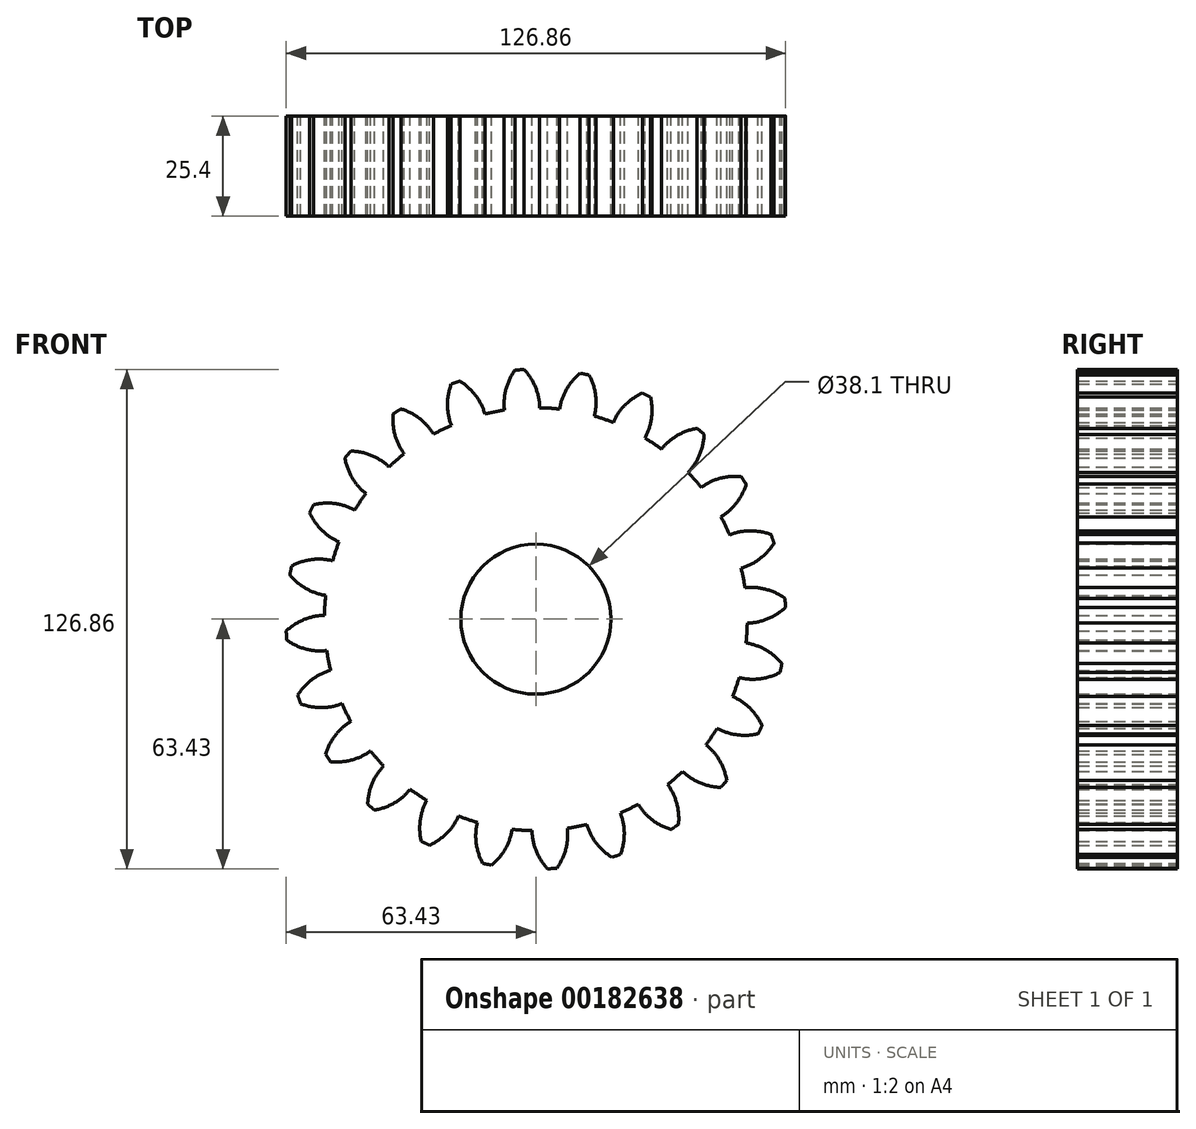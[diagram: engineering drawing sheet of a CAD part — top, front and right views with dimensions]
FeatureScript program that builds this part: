
annotation { "Feature Type Name" : "Feature", "Feature Type Description" : "" }
export const myFeature = defineFeature(function(context is Context, id is Id, definition is map)
    precondition{}
    {
        {
            var Q0;
            Q0=qCreatedBy(makeId("Front.planeOp"),FACE);
            var sketch = newSketch(context, id + "F0", { "sketchPlane" : qUnion([Q0])});
            skCircle(sketch, "E0", {"center": v(0, 0) * mm, "radius": 53.72 * mm});
            skCircle(sketch, "E1", {"center": v(0, 0) * mm, "radius": 58.67 * mm, "construction": true});
            skCircle(sketch, "E2", {"center": v(0, 0) * mm, "radius": 63.5 * mm, "construction": true});
            skLineSegment(sketch, "E3", {"start": v(0, 0) * mm, "end": v(0, 120.36) * mm, "construction": true});
            skLineSegment(sketch, "E4", {"start": v(0, 0) * mm, "end": v(-7.89, 120.36) * mm, "construction": true});
            skLineSegment(sketch, "E5", {"start": v(0, 58.67) * mm, "end": v(-98.12, 58.67) * mm, "construction": true});
            skLineSegment(sketch, "E6", {"start": v(0, 58.67) * mm, "end": v(-98.12, 22.96) * mm, "construction": true});
            skCircle(sketch, "E7", {"center": v(0, 0) * mm, "radius": 55.14 * mm, "construction": true});
            skCircle(sketch, "E8", {"center": v(0, 58.67) * mm, "radius": 14.6 * mm, "construction": true});
            skCircle(sketch, "E9", {"center": v(-13.63, 53.42) * mm, "radius": 14.6 * mm, "construction": true});
            skArc(sketch, "E10", {"start": v(0, 58.67) * mm, "mid": v(-1.27, 61.2) * mm, "end": v(-2.99, 63.43) * mm});
            skArc(sketch, "E11", {"start": v(0.97, 53.71) * mm, "mid": v(0.71, 56.24) * mm, "end": v(0, 58.67) * mm});
            skArc(sketch, "E12.MirrorCS", {"start": v(-7.98, 53.13) * mm, "mid": v(-8.05, 55.66) * mm, "end": v(-7.66, 58.17) * mm});
            skArc(sketch, "E13.MirrorCS", {"start": v(-7.66, 58.17) * mm, "mid": v(-6.72, 60.83) * mm, "end": v(-5.32, 63.28) * mm});
            skArc(sketch, "E14", {"start": v(-2.99, 63.43) * mm, "mid": v(-4.15, 63.36) * mm, "end": v(-5.32, 63.28) * mm});
            skSolve(sketch);
        }
        {
            var Q0;
            Q0=makeQuery(id+"F0.imprint","IMPRINT",FACE,{"disambiguationData":[TD([[makeQuery(id+"F0.imprint","IMPRINT",EDGE,{"derivedFrom":sQuery(id+"F0.wireOp",EDGE,"E10")}),1.0]])]});
            var Q1;
            {var subQ0=sQuery(id+"F0.wireOp",EDGE,"E0");var subQ1=makeQuery(id+"F0.imprint","INTERSECT",VERTEX,{"derivedFrom":[subQ0,sQuery(id+"F0.wireOp",EDGE,"E11")]});Q1=makeQuery(id+"F0.imprint","IMPRINT",FACE,{"disambiguationData":[TD([[makeQuery(id+"F0.imprint","IMPRINT",EDGE,{"disambiguationData":[TD([[subQ1,-1.0]])],"derivedFrom":subQ0}),1.0]])]});}
            extrude(context, id + "F1", {"entities" : qUnion([Q0, Q1]), "depth" : 25.4 * mm});
        }
        {
            var Q0;
            Q0=makeQuery(id+"F1.opExtrude","SWEPT_BODY",BODY,{"disambiguationData":[OSD([sQuery(id+"F0.wireOp",EDGE,"E0"),sQuery(id+"F0.wireOp",EDGE,"E10"),sQuery(id+"F0.wireOp",EDGE,"E11"),sQuery(id+"F0.wireOp",EDGE,"E12.MirrorCS"),sQuery(id+"F0.wireOp",EDGE,"E13.MirrorCS"),sQuery(id+"F0.wireOp",EDGE,"E14")])]});
            var Q1;
            Q1=makeQuery(id+"F1.opExtrude","SWEPT_FACE",FACE,{"disambiguationData":[OSD([sQuery(id+"F0.wireOp",EDGE,"E0")])]});
            circularPattern(context, id + "F2", {"entities" : qUnion([Q0]), "axis" : qUnion([Q1]), "angle" : 15 * degree, "instanceCount" : 24});
        }
        {
            var Q0;
            Q0=makeQuery(id+"F1.opExtrude","SWEPT_BODY",BODY,{"disambiguationData":[OSD([sQuery(id+"F0.wireOp",EDGE,"E0"),sQuery(id+"F0.wireOp",EDGE,"E10"),sQuery(id+"F0.wireOp",EDGE,"E11"),sQuery(id+"F0.wireOp",EDGE,"E12.MirrorCS"),sQuery(id+"F0.wireOp",EDGE,"E13.MirrorCS"),sQuery(id+"F0.wireOp",EDGE,"E14")])]});
            var Q1;
            Q1=makeQuery(id+"F2.opPattern","COPY",BODY,{"derivedFrom":makeQuery(id+"F1.opExtrude","SWEPT_BODY",BODY,{"disambiguationData":[OSD([sQuery(id+"F0.wireOp",EDGE,"E0"),sQuery(id+"F0.wireOp",EDGE,"E10"),sQuery(id+"F0.wireOp",EDGE,"E11"),sQuery(id+"F0.wireOp",EDGE,"E12.MirrorCS"),sQuery(id+"F0.wireOp",EDGE,"E13.MirrorCS"),sQuery(id+"F0.wireOp",EDGE,"E14")])]}),"instanceName":"1"});
            var Q2;
            Q2=makeQuery(id+"F2.opPattern","COPY",BODY,{"derivedFrom":makeQuery(id+"F1.opExtrude","SWEPT_BODY",BODY,{"disambiguationData":[OSD([sQuery(id+"F0.wireOp",EDGE,"E0"),sQuery(id+"F0.wireOp",EDGE,"E10"),sQuery(id+"F0.wireOp",EDGE,"E11"),sQuery(id+"F0.wireOp",EDGE,"E12.MirrorCS"),sQuery(id+"F0.wireOp",EDGE,"E13.MirrorCS"),sQuery(id+"F0.wireOp",EDGE,"E14")])]}),"instanceName":"2"});
            var Q3;
            Q3=makeQuery(id+"F2.opPattern","COPY",BODY,{"derivedFrom":makeQuery(id+"F1.opExtrude","SWEPT_BODY",BODY,{"disambiguationData":[OSD([sQuery(id+"F0.wireOp",EDGE,"E0"),sQuery(id+"F0.wireOp",EDGE,"E10"),sQuery(id+"F0.wireOp",EDGE,"E11"),sQuery(id+"F0.wireOp",EDGE,"E12.MirrorCS"),sQuery(id+"F0.wireOp",EDGE,"E13.MirrorCS"),sQuery(id+"F0.wireOp",EDGE,"E14")])]}),"instanceName":"3"});
            var Q4;
            Q4=makeQuery(id+"F2.opPattern","COPY",BODY,{"derivedFrom":makeQuery(id+"F1.opExtrude","SWEPT_BODY",BODY,{"disambiguationData":[OSD([sQuery(id+"F0.wireOp",EDGE,"E0"),sQuery(id+"F0.wireOp",EDGE,"E10"),sQuery(id+"F0.wireOp",EDGE,"E11"),sQuery(id+"F0.wireOp",EDGE,"E12.MirrorCS"),sQuery(id+"F0.wireOp",EDGE,"E13.MirrorCS"),sQuery(id+"F0.wireOp",EDGE,"E14")])]}),"instanceName":"4"});
            var Q5;
            Q5=makeQuery(id+"F2.opPattern","COPY",BODY,{"derivedFrom":makeQuery(id+"F1.opExtrude","SWEPT_BODY",BODY,{"disambiguationData":[OSD([sQuery(id+"F0.wireOp",EDGE,"E0"),sQuery(id+"F0.wireOp",EDGE,"E10"),sQuery(id+"F0.wireOp",EDGE,"E11"),sQuery(id+"F0.wireOp",EDGE,"E12.MirrorCS"),sQuery(id+"F0.wireOp",EDGE,"E13.MirrorCS"),sQuery(id+"F0.wireOp",EDGE,"E14")])]}),"instanceName":"5"});
            var Q6;
            Q6=makeQuery(id+"F2.opPattern","COPY",BODY,{"derivedFrom":makeQuery(id+"F1.opExtrude","SWEPT_BODY",BODY,{"disambiguationData":[OSD([sQuery(id+"F0.wireOp",EDGE,"E0"),sQuery(id+"F0.wireOp",EDGE,"E10"),sQuery(id+"F0.wireOp",EDGE,"E11"),sQuery(id+"F0.wireOp",EDGE,"E12.MirrorCS"),sQuery(id+"F0.wireOp",EDGE,"E13.MirrorCS"),sQuery(id+"F0.wireOp",EDGE,"E14")])]}),"instanceName":"6"});
            var Q7;
            Q7=makeQuery(id+"F2.opPattern","COPY",BODY,{"derivedFrom":makeQuery(id+"F1.opExtrude","SWEPT_BODY",BODY,{"disambiguationData":[OSD([sQuery(id+"F0.wireOp",EDGE,"E0"),sQuery(id+"F0.wireOp",EDGE,"E10"),sQuery(id+"F0.wireOp",EDGE,"E11"),sQuery(id+"F0.wireOp",EDGE,"E12.MirrorCS"),sQuery(id+"F0.wireOp",EDGE,"E13.MirrorCS"),sQuery(id+"F0.wireOp",EDGE,"E14")])]}),"instanceName":"7"});
            var Q8;
            Q8=makeQuery(id+"F2.opPattern","COPY",BODY,{"derivedFrom":makeQuery(id+"F1.opExtrude","SWEPT_BODY",BODY,{"disambiguationData":[OSD([sQuery(id+"F0.wireOp",EDGE,"E0"),sQuery(id+"F0.wireOp",EDGE,"E10"),sQuery(id+"F0.wireOp",EDGE,"E11"),sQuery(id+"F0.wireOp",EDGE,"E12.MirrorCS"),sQuery(id+"F0.wireOp",EDGE,"E13.MirrorCS"),sQuery(id+"F0.wireOp",EDGE,"E14")])]}),"instanceName":"8"});
            var Q9;
            Q9=makeQuery(id+"F2.opPattern","COPY",BODY,{"derivedFrom":makeQuery(id+"F1.opExtrude","SWEPT_BODY",BODY,{"disambiguationData":[OSD([sQuery(id+"F0.wireOp",EDGE,"E0"),sQuery(id+"F0.wireOp",EDGE,"E10"),sQuery(id+"F0.wireOp",EDGE,"E11"),sQuery(id+"F0.wireOp",EDGE,"E12.MirrorCS"),sQuery(id+"F0.wireOp",EDGE,"E13.MirrorCS"),sQuery(id+"F0.wireOp",EDGE,"E14")])]}),"instanceName":"9"});
            var Q10;
            Q10=makeQuery(id+"F2.opPattern","COPY",BODY,{"derivedFrom":makeQuery(id+"F1.opExtrude","SWEPT_BODY",BODY,{"disambiguationData":[OSD([sQuery(id+"F0.wireOp",EDGE,"E0"),sQuery(id+"F0.wireOp",EDGE,"E10"),sQuery(id+"F0.wireOp",EDGE,"E11"),sQuery(id+"F0.wireOp",EDGE,"E12.MirrorCS"),sQuery(id+"F0.wireOp",EDGE,"E13.MirrorCS"),sQuery(id+"F0.wireOp",EDGE,"E14")])]}),"instanceName":"10"});
            var Q11;
            Q11=makeQuery(id+"F2.opPattern","COPY",BODY,{"derivedFrom":makeQuery(id+"F1.opExtrude","SWEPT_BODY",BODY,{"disambiguationData":[OSD([sQuery(id+"F0.wireOp",EDGE,"E0"),sQuery(id+"F0.wireOp",EDGE,"E10"),sQuery(id+"F0.wireOp",EDGE,"E11"),sQuery(id+"F0.wireOp",EDGE,"E12.MirrorCS"),sQuery(id+"F0.wireOp",EDGE,"E13.MirrorCS"),sQuery(id+"F0.wireOp",EDGE,"E14")])]}),"instanceName":"11"});
            var Q12;
            Q12=makeQuery(id+"F2.opPattern","COPY",BODY,{"derivedFrom":makeQuery(id+"F1.opExtrude","SWEPT_BODY",BODY,{"disambiguationData":[OSD([sQuery(id+"F0.wireOp",EDGE,"E0"),sQuery(id+"F0.wireOp",EDGE,"E10"),sQuery(id+"F0.wireOp",EDGE,"E11"),sQuery(id+"F0.wireOp",EDGE,"E12.MirrorCS"),sQuery(id+"F0.wireOp",EDGE,"E13.MirrorCS"),sQuery(id+"F0.wireOp",EDGE,"E14")])]}),"instanceName":"12"});
            var Q13;
            Q13=makeQuery(id+"F2.opPattern","COPY",BODY,{"derivedFrom":makeQuery(id+"F1.opExtrude","SWEPT_BODY",BODY,{"disambiguationData":[OSD([sQuery(id+"F0.wireOp",EDGE,"E0"),sQuery(id+"F0.wireOp",EDGE,"E10"),sQuery(id+"F0.wireOp",EDGE,"E11"),sQuery(id+"F0.wireOp",EDGE,"E12.MirrorCS"),sQuery(id+"F0.wireOp",EDGE,"E13.MirrorCS"),sQuery(id+"F0.wireOp",EDGE,"E14")])]}),"instanceName":"13"});
            var Q14;
            Q14=makeQuery(id+"F2.opPattern","COPY",BODY,{"derivedFrom":makeQuery(id+"F1.opExtrude","SWEPT_BODY",BODY,{"disambiguationData":[OSD([sQuery(id+"F0.wireOp",EDGE,"E0"),sQuery(id+"F0.wireOp",EDGE,"E10"),sQuery(id+"F0.wireOp",EDGE,"E11"),sQuery(id+"F0.wireOp",EDGE,"E12.MirrorCS"),sQuery(id+"F0.wireOp",EDGE,"E13.MirrorCS"),sQuery(id+"F0.wireOp",EDGE,"E14")])]}),"instanceName":"14"});
            var Q15;
            Q15=makeQuery(id+"F2.opPattern","COPY",BODY,{"derivedFrom":makeQuery(id+"F1.opExtrude","SWEPT_BODY",BODY,{"disambiguationData":[OSD([sQuery(id+"F0.wireOp",EDGE,"E0"),sQuery(id+"F0.wireOp",EDGE,"E10"),sQuery(id+"F0.wireOp",EDGE,"E11"),sQuery(id+"F0.wireOp",EDGE,"E12.MirrorCS"),sQuery(id+"F0.wireOp",EDGE,"E13.MirrorCS"),sQuery(id+"F0.wireOp",EDGE,"E14")])]}),"instanceName":"15"});
            var Q16;
            Q16=makeQuery(id+"F2.opPattern","COPY",BODY,{"derivedFrom":makeQuery(id+"F1.opExtrude","SWEPT_BODY",BODY,{"disambiguationData":[OSD([sQuery(id+"F0.wireOp",EDGE,"E0"),sQuery(id+"F0.wireOp",EDGE,"E10"),sQuery(id+"F0.wireOp",EDGE,"E11"),sQuery(id+"F0.wireOp",EDGE,"E12.MirrorCS"),sQuery(id+"F0.wireOp",EDGE,"E13.MirrorCS"),sQuery(id+"F0.wireOp",EDGE,"E14")])]}),"instanceName":"16"});
            var Q17;
            Q17=makeQuery(id+"F2.opPattern","COPY",BODY,{"derivedFrom":makeQuery(id+"F1.opExtrude","SWEPT_BODY",BODY,{"disambiguationData":[OSD([sQuery(id+"F0.wireOp",EDGE,"E0"),sQuery(id+"F0.wireOp",EDGE,"E10"),sQuery(id+"F0.wireOp",EDGE,"E11"),sQuery(id+"F0.wireOp",EDGE,"E12.MirrorCS"),sQuery(id+"F0.wireOp",EDGE,"E13.MirrorCS"),sQuery(id+"F0.wireOp",EDGE,"E14")])]}),"instanceName":"17"});
            var Q18;
            Q18=makeQuery(id+"F2.opPattern","COPY",BODY,{"derivedFrom":makeQuery(id+"F1.opExtrude","SWEPT_BODY",BODY,{"disambiguationData":[OSD([sQuery(id+"F0.wireOp",EDGE,"E0"),sQuery(id+"F0.wireOp",EDGE,"E10"),sQuery(id+"F0.wireOp",EDGE,"E11"),sQuery(id+"F0.wireOp",EDGE,"E12.MirrorCS"),sQuery(id+"F0.wireOp",EDGE,"E13.MirrorCS"),sQuery(id+"F0.wireOp",EDGE,"E14")])]}),"instanceName":"18"});
            var Q19;
            Q19=makeQuery(id+"F2.opPattern","COPY",BODY,{"derivedFrom":makeQuery(id+"F1.opExtrude","SWEPT_BODY",BODY,{"disambiguationData":[OSD([sQuery(id+"F0.wireOp",EDGE,"E0"),sQuery(id+"F0.wireOp",EDGE,"E10"),sQuery(id+"F0.wireOp",EDGE,"E11"),sQuery(id+"F0.wireOp",EDGE,"E12.MirrorCS"),sQuery(id+"F0.wireOp",EDGE,"E13.MirrorCS"),sQuery(id+"F0.wireOp",EDGE,"E14")])]}),"instanceName":"19"});
            var Q20;
            Q20=makeQuery(id+"F2.opPattern","COPY",BODY,{"derivedFrom":makeQuery(id+"F1.opExtrude","SWEPT_BODY",BODY,{"disambiguationData":[OSD([sQuery(id+"F0.wireOp",EDGE,"E0"),sQuery(id+"F0.wireOp",EDGE,"E10"),sQuery(id+"F0.wireOp",EDGE,"E11"),sQuery(id+"F0.wireOp",EDGE,"E12.MirrorCS"),sQuery(id+"F0.wireOp",EDGE,"E13.MirrorCS"),sQuery(id+"F0.wireOp",EDGE,"E14")])]}),"instanceName":"20"});
            var Q21;
            Q21=makeQuery(id+"F2.opPattern","COPY",BODY,{"derivedFrom":makeQuery(id+"F1.opExtrude","SWEPT_BODY",BODY,{"disambiguationData":[OSD([sQuery(id+"F0.wireOp",EDGE,"E0"),sQuery(id+"F0.wireOp",EDGE,"E10"),sQuery(id+"F0.wireOp",EDGE,"E11"),sQuery(id+"F0.wireOp",EDGE,"E12.MirrorCS"),sQuery(id+"F0.wireOp",EDGE,"E13.MirrorCS"),sQuery(id+"F0.wireOp",EDGE,"E14")])]}),"instanceName":"21"});
            var Q22;
            Q22=makeQuery(id+"F2.opPattern","COPY",BODY,{"derivedFrom":makeQuery(id+"F1.opExtrude","SWEPT_BODY",BODY,{"disambiguationData":[OSD([sQuery(id+"F0.wireOp",EDGE,"E0"),sQuery(id+"F0.wireOp",EDGE,"E10"),sQuery(id+"F0.wireOp",EDGE,"E11"),sQuery(id+"F0.wireOp",EDGE,"E12.MirrorCS"),sQuery(id+"F0.wireOp",EDGE,"E13.MirrorCS"),sQuery(id+"F0.wireOp",EDGE,"E14")])]}),"instanceName":"22"});
            var Q23;
            Q23=makeQuery(id+"F2.opPattern","COPY",BODY,{"derivedFrom":makeQuery(id+"F1.opExtrude","SWEPT_BODY",BODY,{"disambiguationData":[OSD([sQuery(id+"F0.wireOp",EDGE,"E0"),sQuery(id+"F0.wireOp",EDGE,"E10"),sQuery(id+"F0.wireOp",EDGE,"E11"),sQuery(id+"F0.wireOp",EDGE,"E12.MirrorCS"),sQuery(id+"F0.wireOp",EDGE,"E13.MirrorCS"),sQuery(id+"F0.wireOp",EDGE,"E14")])]}),"instanceName":"23"});
            booleanBodies(context, id + "F3", {"operationType" : BooleanOperationType.UNION, "tools" : qUnion([Q0, Q1, Q2, Q3, Q4, Q5, Q6, Q7, Q8, Q9, Q10, Q11, Q12, Q13, Q14, Q15, Q16, Q17, Q18, Q19, Q20, Q21, Q22, Q23])});
        }
        {
            var Q0;
            {var subQ0=makeQuery(id+"F1.opExtrude","CAP_FACE",FACE,{"disambiguationData":[OSD([sQuery(id+"F0.wireOp",EDGE,"E0"),sQuery(id+"F0.wireOp",EDGE,"E10"),sQuery(id+"F0.wireOp",EDGE,"E11"),sQuery(id+"F0.wireOp",EDGE,"E12.MirrorCS"),sQuery(id+"F0.wireOp",EDGE,"E13.MirrorCS"),sQuery(id+"F0.wireOp",EDGE,"E14")])],"isStart":false});Q0=makeQuery(id+"F3.opBoolean","MERGE",FACE,{"derivedFrom":[subQ0,makeQuery(id+"F2.opPattern","COPY",FACE,{"derivedFrom":subQ0,"instanceName":"1"}),makeQuery(id+"F2.opPattern","COPY",FACE,{"derivedFrom":subQ0,"instanceName":"2"}),makeQuery(id+"F2.opPattern","COPY",FACE,{"derivedFrom":subQ0,"instanceName":"3"}),makeQuery(id+"F2.opPattern","COPY",FACE,{"derivedFrom":subQ0,"instanceName":"4"}),makeQuery(id+"F2.opPattern","COPY",FACE,{"derivedFrom":subQ0,"instanceName":"5"}),makeQuery(id+"F2.opPattern","COPY",FACE,{"derivedFrom":subQ0,"instanceName":"6"}),makeQuery(id+"F2.opPattern","COPY",FACE,{"derivedFrom":subQ0,"instanceName":"7"}),makeQuery(id+"F2.opPattern","COPY",FACE,{"derivedFrom":subQ0,"instanceName":"8"}),makeQuery(id+"F2.opPattern","COPY",FACE,{"derivedFrom":subQ0,"instanceName":"9"}),makeQuery(id+"F2.opPattern","COPY",FACE,{"derivedFrom":subQ0,"instanceName":"10"}),makeQuery(id+"F2.opPattern","COPY",FACE,{"derivedFrom":subQ0,"instanceName":"11"}),makeQuery(id+"F2.opPattern","COPY",FACE,{"derivedFrom":subQ0,"instanceName":"12"}),makeQuery(id+"F2.opPattern","COPY",FACE,{"derivedFrom":subQ0,"instanceName":"13"}),makeQuery(id+"F2.opPattern","COPY",FACE,{"derivedFrom":subQ0,"instanceName":"14"}),makeQuery(id+"F2.opPattern","COPY",FACE,{"derivedFrom":subQ0,"instanceName":"15"}),makeQuery(id+"F2.opPattern","COPY",FACE,{"derivedFrom":subQ0,"instanceName":"16"}),makeQuery(id+"F2.opPattern","COPY",FACE,{"derivedFrom":subQ0,"instanceName":"17"}),makeQuery(id+"F2.opPattern","COPY",FACE,{"derivedFrom":subQ0,"instanceName":"18"}),makeQuery(id+"F2.opPattern","COPY",FACE,{"derivedFrom":subQ0,"instanceName":"19"}),makeQuery(id+"F2.opPattern","COPY",FACE,{"derivedFrom":subQ0,"instanceName":"20"}),makeQuery(id+"F2.opPattern","COPY",FACE,{"derivedFrom":subQ0,"instanceName":"21"}),makeQuery(id+"F2.opPattern","COPY",FACE,{"derivedFrom":subQ0,"instanceName":"22"}),makeQuery(id+"F2.opPattern","COPY",FACE,{"derivedFrom":subQ0,"instanceName":"23"})]});}
            var sketch = newSketch(context, id + "F4", { "sketchPlane" : qUnion([Q0])});
            skCircle(sketch, "E15", {"center": v(0, 0) * mm, "radius": 19.05 * mm});
            skSolve(sketch);
        }
        {
            var Q0;
            Q0 = qSketchRegion(id + "F4", true);
            var Q1;
            Q1=sQuery(id+"F4.wireOp",EDGE,"E15");
            extrude(context, id + "F5", {"entities" : qUnion([Q0]), "operationType" : NewBodyOperationType.REMOVE, "surfaceEntities" : qUnion([Q1]), "depth" : 33.27 * mm, "hasSecondDirection" : true, "secondDirectionOppositeDirection" : true, "secondDirectionDepth" : 30.23 * mm});
        }
    });
